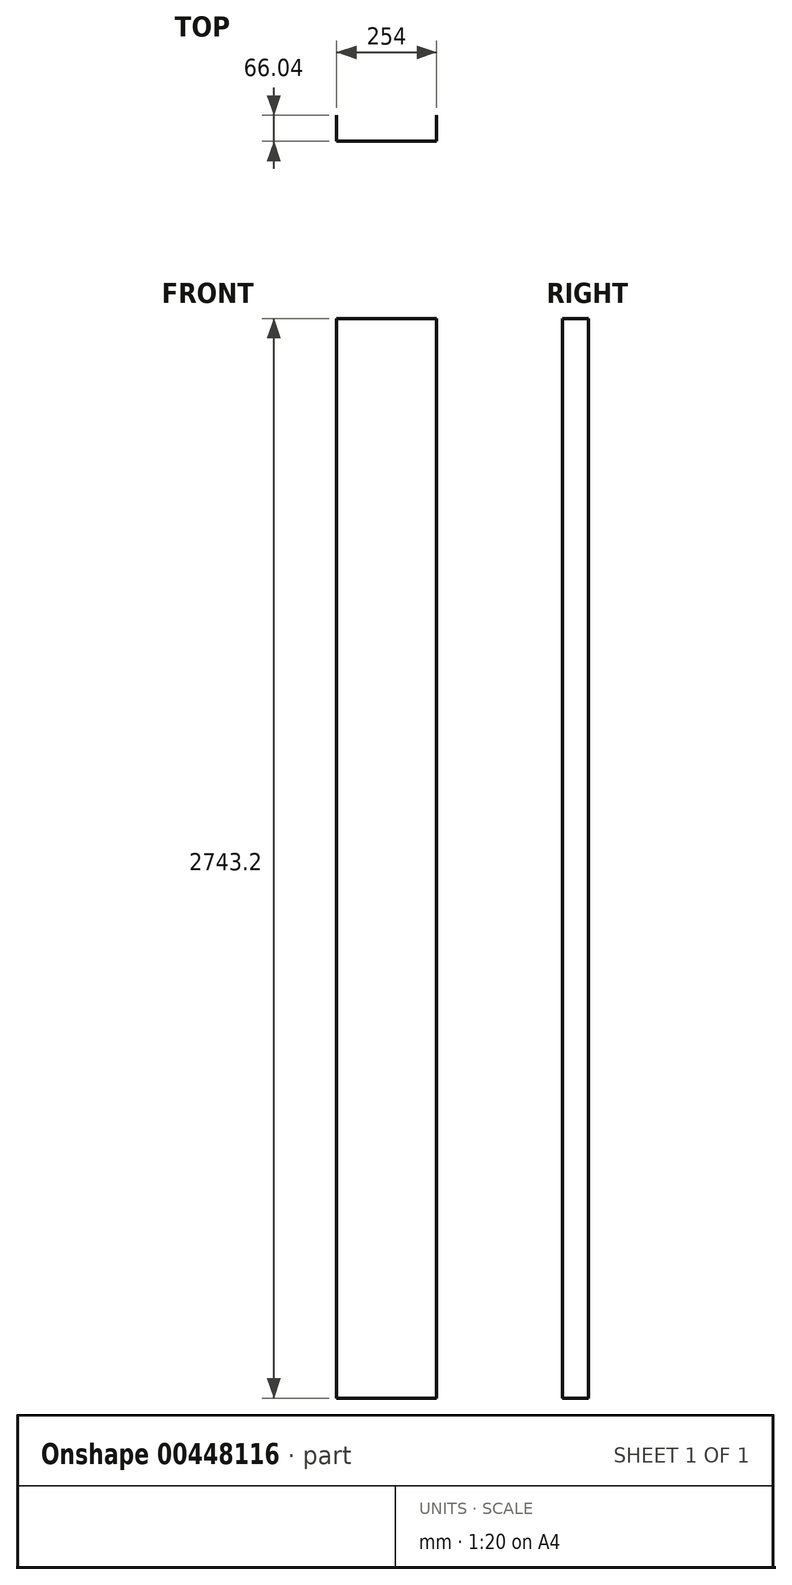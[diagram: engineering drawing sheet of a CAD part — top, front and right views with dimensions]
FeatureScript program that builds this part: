
annotation { "Feature Type Name" : "Feature", "Feature Type Description" : "" }
export const myFeature = defineFeature(function(context is Context, id is Id, definition is map)
    precondition{}
    {
        {
            var Q0;
            Q0=qCreatedBy(makeId("Top.planeOp"),FACE);
            var sketch = newSketch(context, id + "F0", { "sketchPlane" : qUnion([Q0])});
            skLineSegment(sketch, "E0", {"start": v(-127, 66.04) * mm, "end": v(-127, 0) * mm});
            skLineSegment(sketch, "E1", {"start": v(-127, 0) * mm, "end": v(127, 0) * mm});
            skLineSegment(sketch, "E2", {"start": v(127, 0) * mm, "end": v(127, 66.04) * mm});
            skSolve(sketch);
        }
        {
            var Q0;
            Q0 = qSketchRegion(id + "F0", true);
            var Q1;
            Q1=sQuery(id+"F0.wireOp",EDGE,"E1");
            var Q2;
            Q2=sQuery(id+"F0.wireOp",EDGE,"E0");
            var Q3;
            Q3=sQuery(id+"F0.wireOp",EDGE,"E2");
            extrude(context, id + "F1", {"entities" : qUnion([Q0]), "bodyType" : ToolBodyType.SURFACE, "surfaceEntities" : qUnion([Q1, Q2, Q3]), "endBound" : BoundingType.SYMMETRIC, "depth" : 2743.2 * mm});
        }
    });
